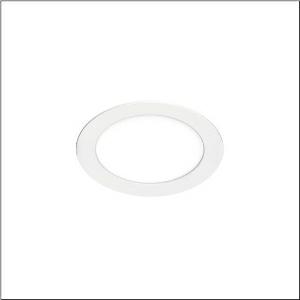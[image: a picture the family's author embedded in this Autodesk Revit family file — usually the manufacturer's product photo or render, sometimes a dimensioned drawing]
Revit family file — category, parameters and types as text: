
# Revit family: lunis_41_flat_51dr10dfgcb
name_source: partatom
category: Lighting Fixtures
units: mm (PartAtom-declared; Revit-internal decimal feet)

## family parameters
Cut with Voids When Loaded = No
Host = Face
Light Source = No
Part Type = Normal
Room Calculation Point = No
Round Connector Dimension = Use Diameter
Shared = No

## types (1)
- --- (1 x LED, 1550 lm, 11.5 W, 4000K)
    Apparent Load = 12 VA
    CIE Flux Codes = 49 80 96 100 100
    Color Rendering = 80
    Color Temperature = 4000K
    Default Elevation = 1800 mm
    Description = Lunis 41 Flat, downlight, light emission: direct distribution, LED rated luminous flux: 3.100lm, light colour: 830/840, control gear: ECG, mains connection: 230V, AC, 50/60Hz, housing, round, of aluminium, coated, traffic white (RAL 9016), diameter: 225mm, protection rating (complete): IP20, protection rating (on room side): IP44, insulation class (complete): insulation class II (safety insulation), certification: CE, permissible ambient temperature for indoor applications: -20..+40°C, packaging unit: 1 piece
    Height = 0 mm  [stored 0 ft]
    Lamp = 1 x LED
    Lamp Light Flux = 1550 lm
    Lamp Power = 11.5 W
    Lamp count = 1
    Length = 225 mm
    Luminous efficacy = 135 lm/W
    Manufacturer = Siteco
    ModVariant = No
    Model = 51DR10DFGCB
    Mounting Place = Ceiling
    Mounting Type = Recessed
    Number of Poles = 1
    OnlyDefault = Yes
    Power Factor = 1
    Product Name = Lunis 41 Flat
    Product group = downlight
    ProductGroupID = 401
    Protection Class = Protection class II
    Protection Degree = IP 20
    RLX_Detail_Level = 1
    RLX_Emergency_Light_Flux = 0 lm
    RLX_Emergency_Type = 0
    RLX_Emergency_Type_DB = No
    RlxData = <blob elided: 13849 chars, md5=b7c010f6>
    Socket = socket
    Standby Power = 0 W
    System Light Flux = 1550 lm
    System Power = 12 W
    Type Comments = factory setting: colour temperature 4000K, luminous flux: 50 % | (ON | ON | ON) | 350 mA
    Type Image = l_1340923.jpg
    URL = http://relux.com
    VarID = @adj_019981
    Voltage = 0 V
    Weight = 0.00 kg
    Width = 0 mm  [stored 0 ft]

note: [stored X ft] marks values corroborated as IEEE doubles in the binary element streams (Revit-internal decimal feet)

## geometry (parser evidence)
native form markers: Sweep x11
no freeform markers — native parametric forms only
